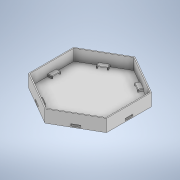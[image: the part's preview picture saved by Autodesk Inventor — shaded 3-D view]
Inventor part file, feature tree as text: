
AUTODESK INVENTOR PART (.ipt)
format: ipt  version: 2020 (Build 240168000, 168)  size: 215,040 bytes
history: native  units: in
note: dims shown in document units (in); Inventor stores cm internally (conversion verified against a paired STEP export)
features: extrude x4, sketch x4, fillet x1, pattern_circular x1
ambient origin geometry x8: Origin, YZ Plane, XZ Plane, XY Plane, X Axis, Y Axis, Z Axis, Center Point
bodies: Solid1 (feature_tree)
feature tree (10):
  extrude  "Extrusion1"  TaperAngle=0.0deg  [1 undecoded]
  extrude  "Extrusion2"  TaperAngle=0.0deg  [1 undecoded]
  sketch  "Sketch4"  dims[d6=3.0709in d7=0.7874in d8=0.0in]
  extrude  "Extrusion3"  Depth=0.7874in TaperAngle=0.0deg
  extrude  "Extrusion4"  Depth=0.128in
  fillet  "Fillet1"  Radius=1.3189in
  pattern_circular  "Circular Pattern1"  [2 undecoded]
  sketch  "Sketch1"  dims[d1=3.1496in d2=0.0in]
  sketch  "Sketch2"  dims[d3=0.8661in d4=0.0in d5=0.0in]
  sketch  "Sketch5"  dims[d9=0.5118in d10=0.128in d11=1.3189in d12=0.6299in d13=0.315in d14=1.2598in d15=0.1575in d16=0.0in d17=0.6299in d18=0.0in d19=0.0394in d20=2.3622in d21=360.0deg]
note: 4 required parameter values undecoded (feature->parameter linkage not recoverable at this tier; creation-order binding heuristic only, values carry confidence <= 0.55)
